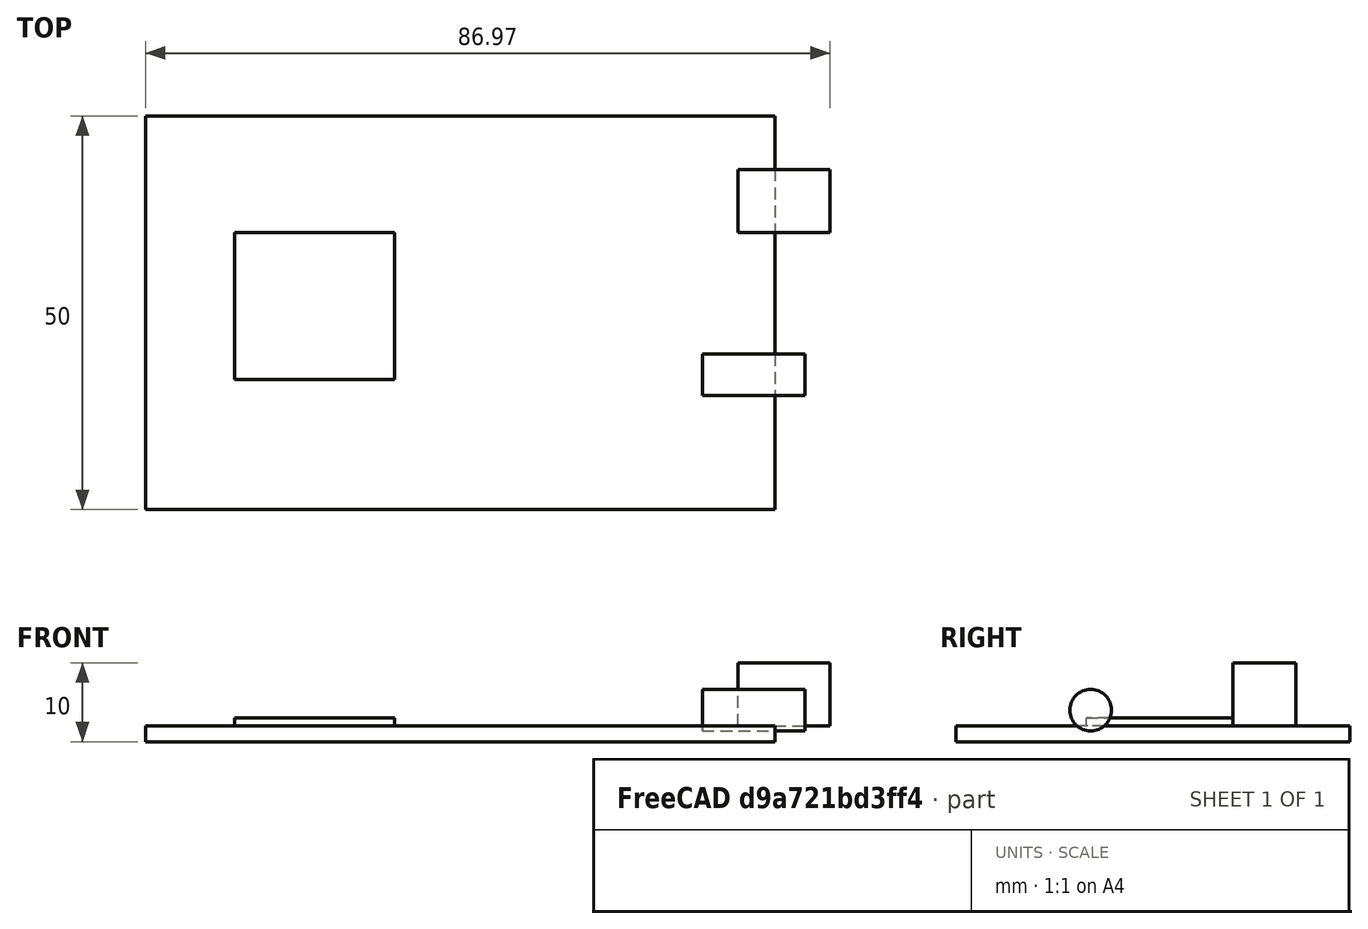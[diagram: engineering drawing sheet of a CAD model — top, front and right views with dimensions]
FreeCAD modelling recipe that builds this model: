
FCSTD DOCUMENT  (FreeCAD 0.19R24291 (Git))
Label: elegoo
License: All rights reserved
LicenseURL: http://en.wikipedia.org/wiki/All_rights_reserved
objects: Sketcher::SketchObject×4, PartDesign::Pad×4, PartDesign::Body×4, TechDraw::DrawProjGroupItem×3, TechDraw::DrawViewDimension×2, PartDesign::Hole×1, App::LinkGroup×1, TechDraw::DrawSVGTemplate×1, TechDraw::DrawProjGroup×1, TechDraw::DrawPage×1
note: 18 computed .brp shape members not serialized (recipe doc carries the construction recipe); baked Part::Feature solids carry a one-line shape summary decoded from their .brp

FEATURE [Sketcher::SketchObject] Sketch
  FullyConstrained = false
  MapMode = 5
  Support = -> [XY_Plane]
  sketch-geometry (4):
    g0: LineSegment StartX=-39.7547 StartY=27.4663 StartZ=0 EndX=40.2453 EndY=27.4663 EndZ=0
    g1: LineSegment StartX=40.2453 StartY=27.4663 StartZ=0 EndX=40.2453 EndY=-22.5337 EndZ=0
    g2: LineSegment StartX=40.2453 StartY=-22.5337 StartZ=0 EndX=-39.7547 EndY=-22.5337 EndZ=0
    g3: LineSegment StartX=-39.7547 StartY=-22.5337 StartZ=0 EndX=-39.7547 EndY=27.4663 EndZ=0
  constraints (10):
    c: Coincident(g0,g1)
    c: Coincident(g1,g2)
    c: Coincident(g2,g3)
    c: Coincident(g3,g0)
    c: Horizontal(g0)
    c: Horizontal(g2)
    c: Vertical(g1)
    c: Vertical(g3)
    c: DistanceX(g0,g0) = 80
    c: DistanceY(g1,g1) = 50
FEATURE [PartDesign::Pad] Pad
  Direction = (1,1,1)
  Length = 2
  Length2 = 100
  Profile = -> Sketch
  Type = 0
FEATURE [PartDesign::Body] Body  label="base"
  Group = -> [Sketch,Pad]
  Origin = -> Origin
  Tip = -> Pad
FEATURE [Sketcher::SketchObject] Sketch001
  FullyConstrained = false
  MapMode = 5
  Support = -> [XY_Plane001]
  sketch-geometry (4):
    g0: LineSegment StartX=59.5865 StartY=-13.365 StartZ=0 EndX=79.8925 EndY=-13.365 EndZ=0
    g1: LineSegment StartX=79.8925 StartY=-13.365 StartZ=0 EndX=79.8925 EndY=-32.002 EndZ=0
    g2: LineSegment StartX=79.8925 StartY=-32.002 StartZ=0 EndX=59.5865 EndY=-32.002 EndZ=0
    g3: LineSegment StartX=59.5865 StartY=-32.002 StartZ=0 EndX=59.5865 EndY=-13.365 EndZ=0
  constraints (8):
    c: Coincident(g0,g1)
    c: Coincident(g1,g2)
    c: Coincident(g2,g3)
    c: Coincident(g3,g0)
    c: Horizontal(g0)
    c: Horizontal(g2)
    c: Vertical(g1)
    c: Vertical(g3)
FEATURE [PartDesign::Pad] Pad001
  Direction = (1,1,1)
  Length = 1
  Length2 = 100
  Profile = -> Sketch001
  Type = 0
FEATURE [PartDesign::Body] Body001  label="chip"
  Group = -> [Sketch001,Pad001]
  Origin = -> Origin001
  Placement = pos=(-88,26,2) rot=(0,0,1;0rad)
  Tip = -> Pad001
FEATURE [Sketcher::SketchObject] Sketch002
  FullyConstrained = false
  MapMode = 5
  Support = -> [XY_Plane002]
  sketch-geometry (4):
    g0: LineSegment StartX=46.5283 StartY=3.66319 StartZ=0 EndX=58.2184 EndY=3.66319 EndZ=0
    g1: LineSegment StartX=58.2184 StartY=3.66319 StartZ=0 EndX=58.2184 EndY=-4.34671 EndZ=0
    g2: LineSegment StartX=58.2184 StartY=-4.34671 StartZ=0 EndX=46.5283 EndY=-4.34671 EndZ=0
    g3: LineSegment StartX=46.5283 StartY=-4.34671 StartZ=0 EndX=46.5283 EndY=3.66319 EndZ=0
  constraints (8):
    c: Coincident(g0,g1)
    c: Coincident(g1,g2)
    c: Coincident(g2,g3)
    c: Coincident(g3,g0)
    c: Horizontal(g0)
    c: Horizontal(g2)
    c: Vertical(g1)
    c: Vertical(g3)
FEATURE [PartDesign::Pad] Pad002
  Direction = (1,1,1)
  Length = 8
  Length2 = 100
  Profile = -> Sketch002
  Type = 0
FEATURE [PartDesign::Hole] Hole
  BaseFeature = -> Pad002
  Depth = 25
  DepthType = 0
  Diameter = 6
  DrillForDepth = false
  DrillPoint = 1
  DrillPointAngle = 118
  HoleCutCountersinkAngle = 90
  HoleCutCustomValues = false
  HoleCutDepth = 0
  HoleCutDiameter = 6.1
  HoleCutType = 0
  ModelActualThread = false
  Profile = -> Pad002
  Tapered = false
  TaperedAngle = 90
  ThreadAngle = 0
  ThreadClass = 0
  ThreadCutOffInner = 0
  ThreadCutOffOuter = 0
  ThreadDirection = 0
  ThreadFit = 0
  ThreadPitch = 0
  ThreadSize = 0
  ThreadType = 0
  Threaded = false
FEATURE [PartDesign::Body] Body002  label="conect"
  Group = -> [Sketch002,Pad002,Hole]
  Origin = -> Origin002
  Placement = pos=(-11,17,2) rot=(0,0,1;0rad)
  Tip = -> Hole
FEATURE [Sketcher::SketchObject] Sketch003
  FullyConstrained = false
  MapMode = 5
  Support = -> [XY_Plane003]
  sketch-geometry (1):
    g0: Circle CenterX=75.4358 CenterY=0 CenterZ=0 NormalX=0 NormalY=0 NormalZ=1 AngleXU=0 Radius=2.64986
  constraints (1):
    c: PointOnObject(g0,g-1)
FEATURE [PartDesign::Pad] Pad003
  Direction = (1,1,1)
  Length = 13
  Length2 = 100
  Profile = -> Sketch003
  Type = 0
FEATURE [PartDesign::Body] Body003  label="bateria"
  Group = -> [Sketch003,Pad003]
  Origin = -> Origin003
  Placement = pos=(44,70,4) rot=(0.57735,-0.57735,-0.57735;2.0944rad)
  Tip = -> Pad003
FEATURE [App::LinkGroup] LinkGroup  label="ardu"
  ElementList = -> [Body003,Body002,Body001,Body]
  LinkMode = 0
  Placement = pos=(20,-2.6226e-06,-4.76837e-07) rot=(0,0,1;0rad)
FEATURE [TechDraw::DrawSVGTemplate] Template
  EditableTexts = Designed_by_Name=Designed by Name; Drawing_number=Drawing number; FC-Date=Date; FC-SC=Scale; FC-SH=Sheet; FC-Title=Title; Subtitle=Subtitle; Weight=Weight
  Height = 210
  Orientation = 1
  Width = 297
FEATURE [TechDraw::DrawProjGroupItem] ProjItem  label="Front"
  CoarseView = false
  Direction = (0,0,1)
  Focus = 100
  HardHidden = false
  IsoCount = 0
  IsoHidden = false
  IsoVisible = false
  LockPosition = true
  Perspective = false
  Rotation = 0
  RotationVector = (1,0,0)
  ScaleType = 2
  SeamHidden = false
  SeamVisible = true
  SmoothHidden = false
  SmoothVisible = true
  Type = 0
  X = 0
  XDirection = (1,0,0)
  XSource = -> [LinkGroup]
  Y = 0
FEATURE [TechDraw::DrawProjGroupItem] ProjItem001  label="Left"
  CoarseView = false
  Direction = (-1,0,1e-16)
  Focus = 100
  HardHidden = false
  IsoCount = 0
  IsoHidden = false
  IsoVisible = false
  LockPosition = false
  Perspective = false
  Rotation = 0
  RotationVector = (1,0,0)
  ScaleType = 2
  SeamHidden = false
  SeamVisible = true
  SmoothHidden = false
  SmoothVisible = true
  Type = 1
  X = 63.4865
  XDirection = (1e-16,0,1)
  XSource = -> [LinkGroup]
  Y = 0
FEATURE [TechDraw::DrawProjGroupItem] ProjItem002  label="Bottom"
  CoarseView = false
  Direction = (0,-1,0)
  Focus = 100
  HardHidden = false
  IsoCount = 0
  IsoHidden = false
  IsoVisible = false
  LockPosition = false
  Perspective = false
  Rotation = 0
  RotationVector = (1,0,0)
  ScaleType = 2
  SeamHidden = false
  SeamVisible = true
  SmoothHidden = false
  SmoothVisible = true
  Type = 5
  X = 0
  XDirection = (1,0,0)
  XSource = -> [LinkGroup]
  Y = 45
FEATURE [TechDraw::DrawProjGroup] ProjGroup
  Anchor = -> ProjItem
  AutoDistribute = true
  LockPosition = false
  ProjectionType = 0
  Rotation = 0
  ScaleType = 0
  Views = -> [ProjItem,ProjItem001,ProjItem002]
  X = 122.287
  XSource = -> [LinkGroup]
  Y = 107.062
  spacingX = 15
  spacingY = 15
FEATURE [TechDraw::DrawViewDimension] Dimension
  Arbitrary = false
  ArbitraryTolerances = false
  EqualTolerance = true
  FormatSpec = %.2f
  FormatSpecOverTolerance = %+.2f
  FormatSpecUnderTolerance = %+.2f
  Inverted = false
  LockPosition = false
  MeasureType = 1
  OverTolerance = 0
  References2D = -> [ProjItem]
  Rotation = 0
  ScaleType = 0
  TheoreticalExact = false
  Type = 1
  UnderTolerance = 0
  X = -3.48655
  Y = -25
FEATURE [TechDraw::DrawViewDimension] Dimension001
  Arbitrary = false
  ArbitraryTolerances = false
  EqualTolerance = true
  FormatSpec = %.2f
  FormatSpecOverTolerance = %+.2f
  FormatSpecUnderTolerance = %+.2f
  Inverted = false
  LockPosition = false
  MeasureType = 1
  OverTolerance = 0
  References2D = -> [ProjItem]
  Rotation = 0
  ScaleType = 0
  TheoreticalExact = false
  Type = 2
  UnderTolerance = 0
  X = -56.7404
  Y = 2.06171
FEATURE [TechDraw::DrawPage] Page
  KeepUpdated = true
  NextBalloonIndex = 1
  ProjectionType = 0
  Template = -> Template
  Views = -> [ProjGroup,Dimension,Dimension001]
